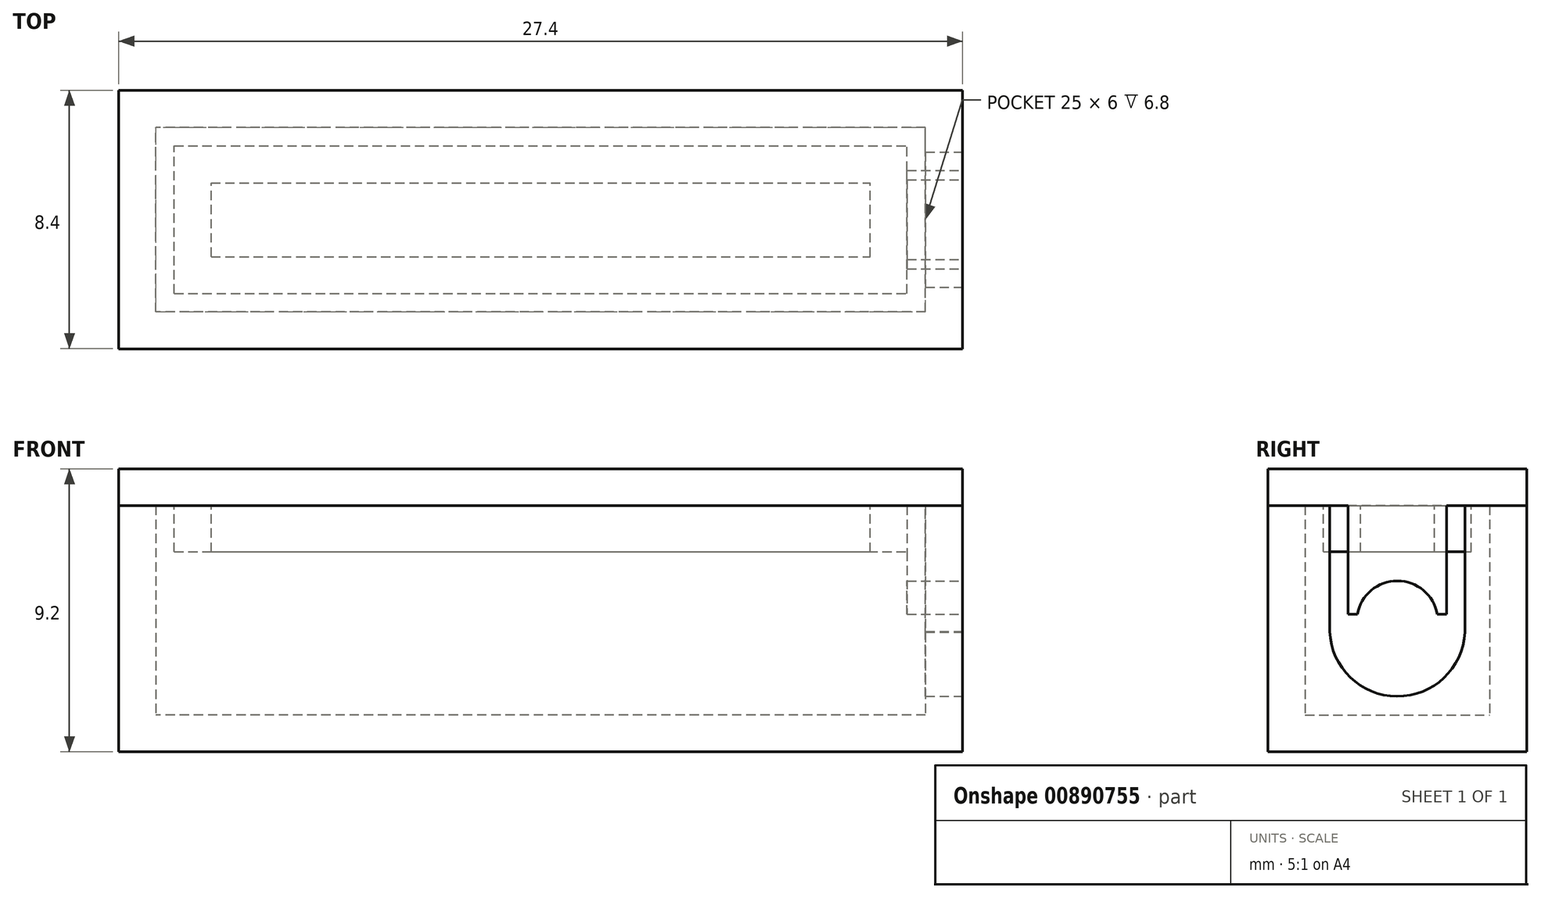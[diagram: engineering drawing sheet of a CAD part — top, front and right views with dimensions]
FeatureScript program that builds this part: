
annotation { "Feature Type Name" : "Feature", "Feature Type Description" : "" }
export const myFeature = defineFeature(function(context is Context, id is Id, definition is map)
    precondition{}
    {
        {
            assignVariable(context, id + "F0", {"name" : "wall", "anyValue" : 1.2});
        }
        {
            var Q0;
            Q0=qCreatedBy(makeId("Top.planeOp"),FACE);
            var sketch = newSketch(context, id + "F1", { "sketchPlane" : qUnion([Q0])});
            skLineSegment(sketch, "E0.bottom", {"start": v(5.83, -17.92) * mm, "end": v(-19.17, -17.92) * mm});
            skLineSegment(sketch, "E0.top", {"start": v(5.83, -11.92) * mm, "end": v(-19.17, -11.92) * mm});
            skLineSegment(sketch, "E0.left", {"start": v(5.83, -17.92) * mm, "end": v(5.83, -11.92) * mm});
            skLineSegment(sketch, "E0.right", {"start": v(-19.17, -17.92) * mm, "end": v(-19.17, -11.92) * mm});
            skLineSegment(sketch, "E1.bottom", {"start": v(-20.37, -10.72) * mm, "end": v(7.03, -10.72) * mm});
            skLineSegment(sketch, "E1.top", {"start": v(-20.37, -19.12) * mm, "end": v(7.03, -19.12) * mm});
            skLineSegment(sketch, "E1.left", {"start": v(-20.37, -10.72) * mm, "end": v(-20.37, -19.12) * mm});
            skLineSegment(sketch, "E1.right", {"start": v(7.03, -10.72) * mm, "end": v(7.03, -19.12) * mm});
            skSolve(sketch);
        }
        {
            var Q0;
            Q0=makeQuery(id+"F1.imprint","IMPRINT",FACE,{"disambiguationData":[TD([[makeQuery(id+"F1.imprint","IMPRINT",EDGE,{"derivedFrom":sQuery(id+"F1.wireOp",EDGE,"E0.bottom")}),-1.0]])]});
            extrude(context, id + "F2", {"entities" : qUnion([Q0]), "depth" : getVariable(context, 'wall') * mm, "offsetDistance" : 25 * mm});
        }
        {
            var Q0;
            Q0 = qSketchRegion(id + "F1", true);
            extrude(context, id + "F3", {"entities" : qUnion([Q0]), "operationType" : NewBodyOperationType.ADD, "depth" : 8 * mm, "offsetDistance" : 25 * mm});
        }
        {
            var Q0;
            Q0=makeQuery(id+"F3.opExtrude","SWEPT_FACE",FACE,{"disambiguationData":[OSD([sQuery(id+"F1.wireOp",EDGE,"E1.right")])]});
            var sketch = newSketch(context, id + "F4", { "sketchPlane" : qUnion([Q0])});
            skArc(sketch, "E2", {"start": v(-17.12, 4.09) * mm, "mid": v(-14.91, 1.8) * mm, "end": v(-12.73, 4.12) * mm});
            skLineSegment(sketch, "E3", {"start": v(-12.73, 3.88) * mm, "end": v(-12.73, 8) * mm});
            skLineSegment(sketch, "E4", {"start": v(-17.12, 3.91) * mm, "end": v(-17.12, 8) * mm});
            skLineSegment(sketch, "E5", {"start": v(-17.12, 8) * mm, "end": v(-12.73, 8) * mm});
            skSolve(sketch);
        }
        {
            var Q0;
            {var subQ6=sQuery(id+"F4.wireOp",EDGE,"E5");Q0=makeQuery(id+"F4.imprint","IMPRINT",FACE,{"disambiguationData":[TD([[makeQuery(id+"F4.imprint","IMPRINT",EDGE,{"derivedFrom":subQ6}),1.0]])]});}
            extrude(context, id + "F5", {"entities" : qUnion([Q0]), "operationType" : NewBodyOperationType.REMOVE, "endBound" : BoundingType.UP_TO_NEXT, "oppositeDirection" : true, "depth" : 25 * mm, "offsetDistance" : 25 * mm});
        }
        {
            var Q0;
            Q0=makeQuery(id+"F3.opExtrude","CAP_FACE",FACE,{"disambiguationData":[OSD([sQuery(id+"F1.wireOp",EDGE,"E0.bottom"),sQuery(id+"F1.wireOp",EDGE,"E0.top"),sQuery(id+"F1.wireOp",EDGE,"E0.left"),sQuery(id+"F1.wireOp",EDGE,"E0.right"),sQuery(id+"F1.wireOp",EDGE,"E1.bottom"),sQuery(id+"F1.wireOp",EDGE,"E1.top"),sQuery(id+"F1.wireOp",EDGE,"E1.left"),sQuery(id+"F1.wireOp",EDGE,"E1.right")])],"isStart":false});
            var sketch = newSketch(context, id + "F6", { "sketchPlane" : qUnion([Q0])});
            skLineSegment(sketch, "E6.bottom", {"start": v(-20.37, -10.72) * mm, "end": v(7.03, -10.72) * mm});
            skLineSegment(sketch, "E6.top", {"start": v(-20.37, -19.12) * mm, "end": v(7.03, -19.12) * mm});
            skLineSegment(sketch, "E6.left", {"start": v(-20.37, -10.72) * mm, "end": v(-20.37, -19.12) * mm});
            skLineSegment(sketch, "E6.right", {"start": v(7.03, -10.72) * mm, "end": v(7.03, -19.12) * mm});
            skSolve(sketch);
        }
        {
            var Q0;
            {var subQ11=sQuery(id+"F6.wireOp",EDGE,"E6.bottom");Q0=makeQuery(id+"F6.imprint","IMPRINT",FACE,{"disambiguationData":[TD([[makeQuery(id+"F6.imprint","IMPRINT",EDGE,{"derivedFrom":subQ11}),-1.0]])]});}
            var Q1;
            {var subQ1=sQuery(id+"F1.wireOp",EDGE,"E0.bottom");Q1=makeQuery(id+"F6.imprint","IMPRINT",FACE,{"disambiguationData":[TD([[makeQuery(id+"F6.imprint","IMPRINT",EDGE,{"derivedFrom":makeQuery(id+"F3.opExtrude","CAP_EDGE",EDGE,{"disambiguationData":[OSD([subQ1])],"isStart":false})}),-1.0]])]});}
            extrude(context, id + "F7", {"entities" : qUnion([Q0, Q1]), "depth" : getVariable(context, 'wall') * mm, "offsetDistance" : 25 * mm});
        }
        {
            var Q0;
            Q0=makeQuery(id+"F7.opExtrude","CAP_FACE",FACE,{"disambiguationData":[OSD([sQuery(id+"F6.wireOp",EDGE,"E6.bottom"),sQuery(id+"F6.wireOp",EDGE,"E6.top"),sQuery(id+"F6.wireOp",EDGE,"E6.left"),sQuery(id+"F6.wireOp",EDGE,"E6.right")])],"isStart":true});
            var sketch = newSketch(context, id + "F8", { "sketchPlane" : qUnion([Q0])});
            skLineSegment(sketch, "E7.bottom", {"start": v(5.83, 11.92) * mm, "end": v(-19.17, 11.92) * mm});
            skLineSegment(sketch, "E7.top", {"start": v(5.83, 17.92) * mm, "end": v(-19.17, 17.92) * mm});
            skLineSegment(sketch, "E7.left", {"start": v(5.83, 11.92) * mm, "end": v(5.83, 17.92) * mm});
            skLineSegment(sketch, "E7.right", {"start": v(-19.17, 11.92) * mm, "end": v(-19.17, 17.92) * mm});
            skLineSegment(sketch, "E8.bottom", {"start": v(-20.37, 19.12) * mm, "end": v(7.03, 19.12) * mm});
            skLineSegment(sketch, "E8.top", {"start": v(-20.37, 10.72) * mm, "end": v(7.03, 10.72) * mm});
            skLineSegment(sketch, "E8.left", {"start": v(-20.37, 19.12) * mm, "end": v(-20.37, 10.72) * mm});
            skLineSegment(sketch, "E8.right", {"start": v(7.03, 19.12) * mm, "end": v(7.03, 10.72) * mm});
            skLineSegment(sketch, "E9.bottom", {"start": v(-18.57, 17.32) * mm, "end": v(5.23, 17.32) * mm});
            skLineSegment(sketch, "E9.top", {"start": v(-18.57, 12.52) * mm, "end": v(5.23, 12.52) * mm});
            skLineSegment(sketch, "E9.left", {"start": v(-18.57, 17.32) * mm, "end": v(-18.57, 12.52) * mm});
            skLineSegment(sketch, "E9.right", {"start": v(5.23, 17.32) * mm, "end": v(5.23, 12.52) * mm});
            skLineSegment(sketch, "E10.bottom", {"start": v(-17.37, 16.12) * mm, "end": v(4.03, 16.12) * mm});
            skLineSegment(sketch, "E10.top", {"start": v(-17.37, 13.72) * mm, "end": v(4.03, 13.72) * mm});
            skLineSegment(sketch, "E10.left", {"start": v(-17.37, 16.12) * mm, "end": v(-17.37, 13.72) * mm});
            skLineSegment(sketch, "E10.right", {"start": v(4.03, 16.12) * mm, "end": v(4.03, 13.72) * mm});
            skSolve(sketch);
        }
        {
            var Q0;
            Q0=makeQuery(id+"F8.imprint","IMPRINT",FACE,{"disambiguationData":[TD([[makeQuery(id+"F8.imprint","IMPRINT",EDGE,{"derivedFrom":sQuery(id+"F8.wireOp",EDGE,"E9.bottom")}),-1.0]])]});
            extrude(context, id + "F9", {"entities" : qUnion([Q0]), "operationType" : NewBodyOperationType.ADD, "depth" : 1.5 * mm, "offsetDistance" : 25 * mm});
        }
        {
            var Q0;
            Q0=makeQuery(id+"F7.opExtrude","SWEPT_FACE",FACE,{"disambiguationData":[OSD([sQuery(id+"F6.wireOp",EDGE,"E6.right")])]});
            var sketch = newSketch(context, id + "F10", { "sketchPlane" : qUnion([Q0])});
            skLineSegment(sketch, "E11", {"start": v(-13.33, 4.47) * mm, "end": v(-13.33, 8) * mm});
            skLineSegment(sketch, "E12", {"start": v(-13.33, 8) * mm, "end": v(-16.52, 8) * mm});
            skLineSegment(sketch, "E13.trimOffspring", {"start": v(-16.52, 4.47) * mm, "end": v(-16.52, 8) * mm});
            skArc(sketch, "E14", {"start": v(-13.63, 4.47) * mm, "mid": v(-14.92, 5.56) * mm, "end": v(-16.22, 4.47) * mm});
            skLineSegment(sketch, "E15", {"start": v(-16.52, 4.47) * mm, "end": v(-16.22, 4.47) * mm});
            skLineSegment(sketch, "E16", {"start": v(-13.33, 4.47) * mm, "end": v(-13.63, 4.47) * mm});
            skSolve(sketch);
        }
        {
            var Q0;
            Q0=makeQuery(id+"F10.imprint","IMPRINT",FACE,{"disambiguationData":[TD([[makeQuery(id+"F10.imprint","IMPRINT",EDGE,{"derivedFrom":sQuery(id+"F10.wireOp",EDGE,"E11")}),1.0]])]});
            var Q1;
            Q1=makeQuery(id+"F9.opExtrude","SWEPT_FACE",FACE,{"disambiguationData":[OSD([sQuery(id+"F8.wireOp",EDGE,"E9.right")])]});
            extrude(context, id + "F11", {"entities" : qUnion([Q0]), "operationType" : NewBodyOperationType.ADD, "endBound" : BoundingType.UP_TO_SURFACE, "oppositeDirection" : true, "depth" : 25 * mm, "endBoundEntityFace" : qUnion([Q1]), "offsetDistance" : 25 * mm});
        }
    });
